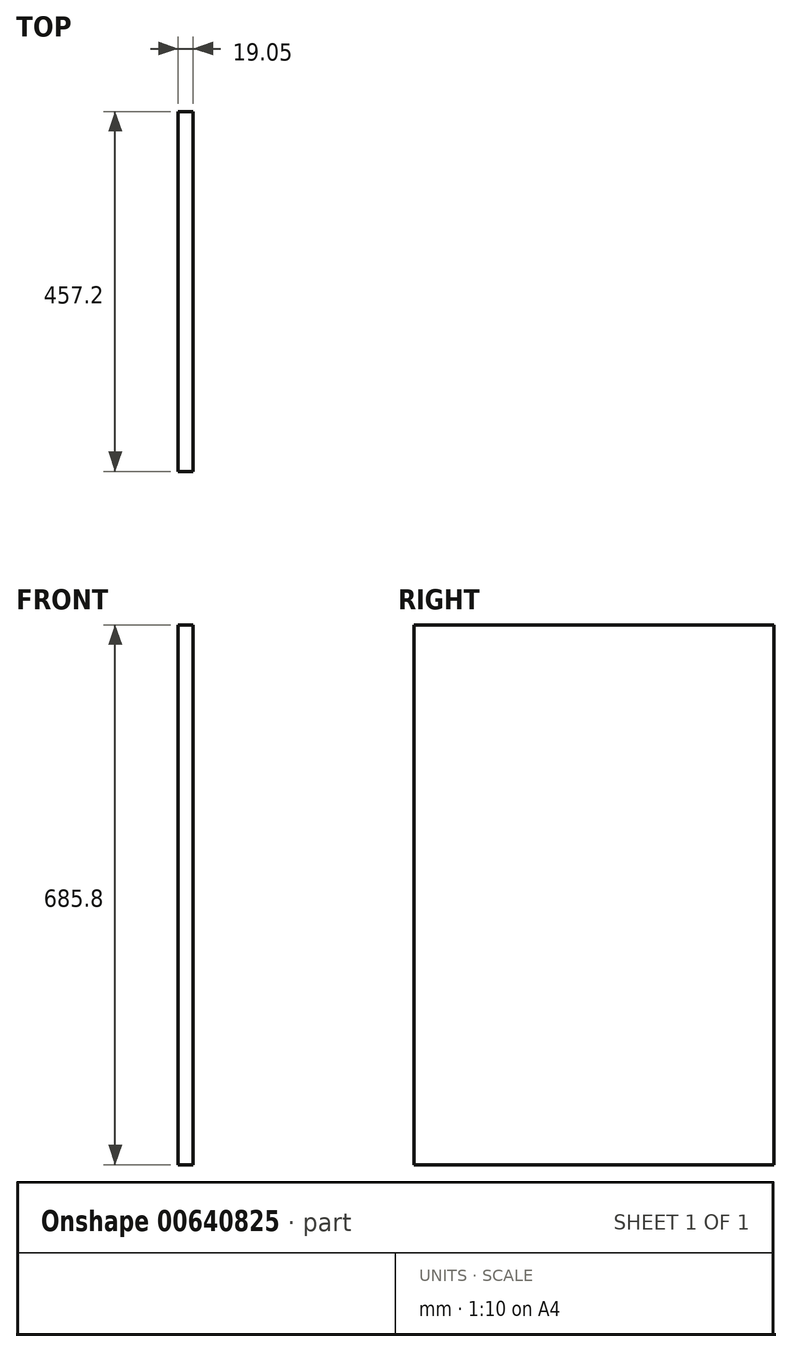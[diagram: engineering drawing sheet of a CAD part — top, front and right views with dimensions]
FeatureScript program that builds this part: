
annotation { "Feature Type Name" : "Feature", "Feature Type Description" : "" }
export const myFeature = defineFeature(function(context is Context, id is Id, definition is map)
    precondition{}
    {
        {
            var Q0;
            Q0=qCreatedBy(makeId("Right.planeOp"),FACE);
            var sketch = newSketch(context, id + "F0", { "sketchPlane" : qUnion([Q0])});
            skLineSegment(sketch, "E0.bottom", {"start": v(228.6, 342.9) * mm, "end": v(-228.6, 342.9) * mm});
            skLineSegment(sketch, "E0.top", {"start": v(228.6, -342.9) * mm, "end": v(-228.6, -342.9) * mm});
            skLineSegment(sketch, "E0.left", {"start": v(228.6, 342.9) * mm, "end": v(228.6, -342.9) * mm});
            skLineSegment(sketch, "E0.right", {"start": v(-228.6, 342.9) * mm, "end": v(-228.6, -342.9) * mm});
            skPoint(sketch, "E0.middle", {"position": v(0, 0) * mm});
            skSolve(sketch);
        }
        {
            var Q0;
            Q0=makeQuery(id+"F0.imprint","IMPRINT",FACE,{"disambiguationData":[TD([[makeQuery(id+"F0.imprint","IMPRINT",EDGE,{"derivedFrom":sQuery(id+"F0.wireOp",EDGE,"E0.bottom")}),1.0]])]});
            extrude(context, id + "F1", {"entities" : qUnion([Q0]), "depth" : 19.05 * mm, "offsetDistance" : 25.4 * mm});
        }
    });
